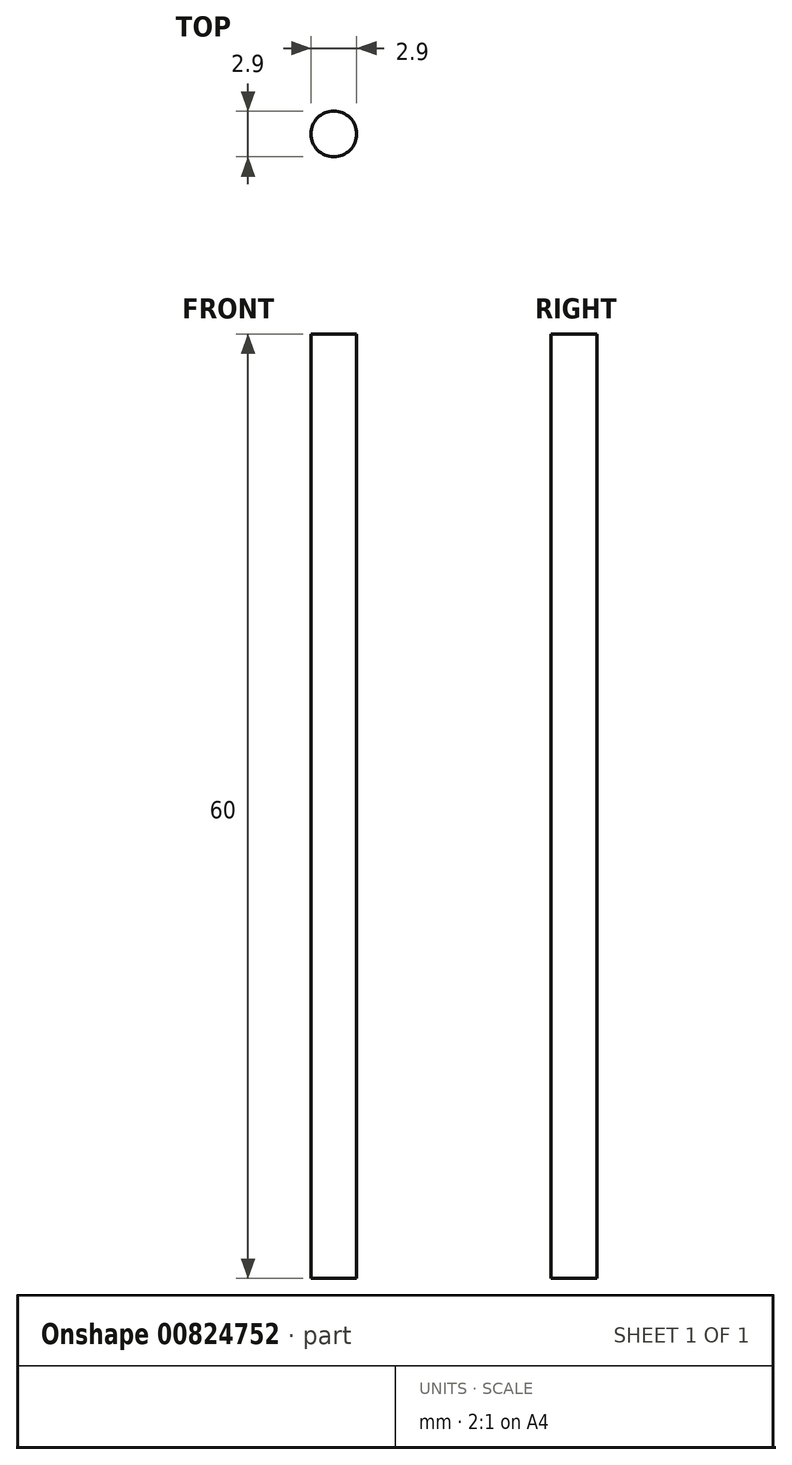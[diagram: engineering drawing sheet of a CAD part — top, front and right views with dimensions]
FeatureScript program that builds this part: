
annotation { "Feature Type Name" : "Feature", "Feature Type Description" : "" }
export const myFeature = defineFeature(function(context is Context, id is Id, definition is map)
    precondition{}
    {
        {
            var Q0;
            Q0=qCreatedBy(makeId("Top.planeOp"),FACE);
            var sketch = newSketch(context, id + "F0", { "sketchPlane" : qUnion([Q0])});
            skCircle(sketch, "E0", {"center": v(0, 0) * mm, "radius": 1.45 * mm});
            skSolve(sketch);
        }
        {
            var Q0;
            Q0=makeQuery(id+"F0.imprint","IMPRINT",FACE,{"disambiguationData":[TD([[makeQuery(id+"F0.imprint","IMPRINT",EDGE,{"derivedFrom":sQuery(id+"F0.wireOp",EDGE,"E0")}),1.0]])]});
            extrude(context, id + "F1", {"entities" : qUnion([Q0]), "depth" : 60 * mm, "offsetDistance" : 25 * mm});
        }
    });
